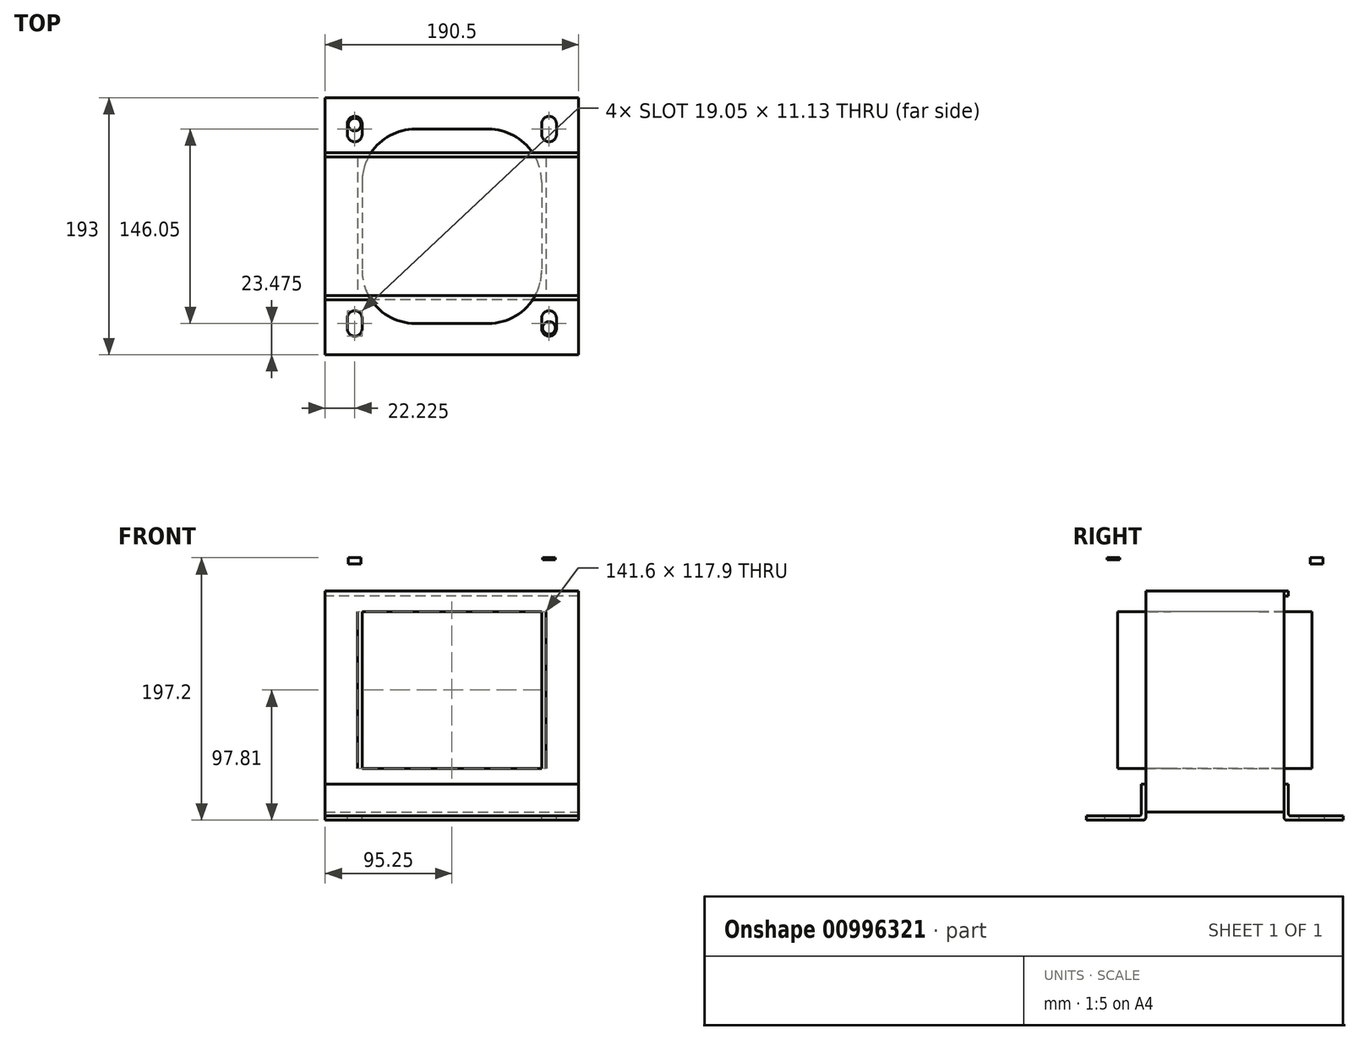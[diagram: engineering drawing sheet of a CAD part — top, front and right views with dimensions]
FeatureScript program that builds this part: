
annotation { "Feature Type Name" : "Feature", "Feature Type Description" : "" }
export const myFeature = defineFeature(function(context is Context, id is Id, definition is map)
    precondition{}
    {
        {
            var Q0;
            Q0=qCreatedBy(makeId("Front.planeOp"),FACE);
            var sketch = newSketch(context, id + "F0", { "sketchPlane" : qUnion([Q0])});
            skLineSegment(sketch, "E0.bottom", {"start": v(-95.25, -91.61) * mm, "end": v(95.25, -91.61) * mm});
            skLineSegment(sketch, "E0.top", {"start": v(-95.25, 91.61) * mm, "end": v(95.25, 91.61) * mm});
            skLineSegment(sketch, "E0.left", {"start": v(-95.25, -91.61) * mm, "end": v(-95.25, 91.61) * mm});
            skLineSegment(sketch, "E0.right", {"start": v(95.25, -91.61) * mm, "end": v(95.25, 91.61) * mm});
            skPoint(sketch, "E0.middle", {"position": v(0, 0) * mm});
            skSolve(sketch);
        }
        {
            var Q0;
            Q0=makeQuery(id+"F0.imprint","IMPRINT",FACE,{"disambiguationData":[TD([[makeQuery(id+"F0.imprint","IMPRINT",EDGE,{"derivedFrom":sQuery(id+"F0.wireOp",EDGE,"E0.bottom")}),1.0]])]});
            extrude(context, id + "F1", {"entities" : qUnion([Q0]), "depth" : 104 * mm, "offsetDistance" : 25 * mm});
        }
        {
            var Q0;
            Q0=makeQuery(id+"F1.opExtrude","SWEPT_FACE",FACE,{"disambiguationData":[OSD([sQuery(id+"F0.wireOp",EDGE,"E0.left")])]});
            var sketch = newSketch(context, id + "F2", { "sketchPlane" : qUnion([Q0])});
            skLineSegment(sketch, "E1.bottom", {"start": v(104, -70.61) * mm, "end": v(107.2, -70.61) * mm});
            skLineSegment(sketch, "E1.left", {"start": v(104, -70.61) * mm, "end": v(104, -94.61) * mm});
            skLineSegment(sketch, "E1.right", {"start": v(107.2, -70.61) * mm, "end": v(107.2, -92.61) * mm});
            skLineSegment(sketch, "E2.bottom", {"start": v(109.2, -94.61) * mm, "end": v(148.5, -94.61) * mm});
            skLineSegment(sketch, "E2.top", {"start": v(106, -97.81) * mm, "end": v(148.5, -97.81) * mm});
            skLineSegment(sketch, "E2.left", {"start": v(104, -94.61) * mm, "end": v(104, -95.81) * mm});
            skLineSegment(sketch, "E2.right", {"start": v(148.5, -94.61) * mm, "end": v(148.5, -97.81) * mm});
            skPoint(sketch, "E3.visualSharp", {"position": v(104, -97.81) * mm});
            skArc(sketch, "E3.filletArc", {"start": v(104, -95.81) * mm, "mid": v(104.59, -97.23) * mm, "end": v(106, -97.82) * mm});
            skPoint(sketch, "E4.visualSharp", {"position": v(107.2, -94.61) * mm});
            skArc(sketch, "E4.filletArc", {"start": v(107.2, -92.61) * mm, "mid": v(107.79, -94.03) * mm, "end": v(109.2, -94.62) * mm});
            skArc(sketch, "E5.MirrorCS", {"start": v(107.2, 92.62) * mm, "mid": v(107.79, 94.03) * mm, "end": v(109.2, 94.62) * mm});
            skArc(sketch, "E6.MirrorCS", {"start": v(104, 95.82) * mm, "mid": v(104.59, 97.23) * mm, "end": v(106, 97.82) * mm});
            skLineSegment(sketch, "E7.MirrorCS", {"start": v(104, 94.62) * mm, "end": v(104, 95.82) * mm});
            skLineSegment(sketch, "E8.MirrorCS", {"start": v(104, 70.62) * mm, "end": v(107.2, 70.62) * mm});
            skLineSegment(sketch, "E9.MirrorCS", {"start": v(148.5, 94.61) * mm, "end": v(148.5, 97.81) * mm});
            skPoint(sketch, "E10.MirrorP", {"position": v(107.2, 94.62) * mm});
            skLineSegment(sketch, "E11.MirrorCS", {"start": v(109.2, 94.62) * mm, "end": v(148.5, 94.61) * mm});
            skLineSegment(sketch, "E12.MirrorCS", {"start": v(104, 70.62) * mm, "end": v(104, 94.62) * mm});
            skLineSegment(sketch, "E13.MirrorCS", {"start": v(106, 97.82) * mm, "end": v(148.5, 97.81) * mm});
            skPoint(sketch, "E14.MirrorP", {"position": v(104, 97.82) * mm});
            skLineSegment(sketch, "E15.MirrorCS", {"start": v(107.2, 70.62) * mm, "end": v(107.2, 92.62) * mm});
            skLineSegment(sketch, "E16", {"start": v(52, 82.48) * mm, "end": v(52, 91.62) * mm, "construction": true});
            skLineSegment(sketch, "E17.MirrorCS", {"start": v(0, 94.62) * mm, "end": v(0, 95.82) * mm});
            skArc(sketch, "E18.MirrorCS", {"start": v(0, 95.82) * mm, "mid": v(-0.59, 97.23) * mm, "end": v(-2, 97.82) * mm});
            skArc(sketch, "E19.MirrorCS", {"start": v(-3.2, 92.62) * mm, "mid": v(-3.79, 94.03) * mm, "end": v(-5.2, 94.62) * mm});
            skLineSegment(sketch, "E20.MirrorCS", {"start": v(0, 70.62) * mm, "end": v(-3.2, 70.62) * mm});
            skLineSegment(sketch, "E21.MirrorCS", {"start": v(-44.5, 94.61) * mm, "end": v(-44.5, 97.81) * mm});
            skPoint(sketch, "E22.MirrorP", {"position": v(0, 97.82) * mm});
            skLineSegment(sketch, "E23.MirrorCS", {"start": v(-5.2, 94.62) * mm, "end": v(-44.5, 94.61) * mm});
            skLineSegment(sketch, "E24.MirrorCS", {"start": v(-3.2, 70.62) * mm, "end": v(-3.2, 92.62) * mm});
            skLineSegment(sketch, "E25.MirrorCS", {"start": v(-2, 97.82) * mm, "end": v(-44.5, 97.81) * mm});
            skLineSegment(sketch, "E26.MirrorCS", {"start": v(0, 70.62) * mm, "end": v(0, 94.62) * mm});
            skPoint(sketch, "E27.MirrorP", {"position": v(-3.2, 94.62) * mm});
            skLineSegment(sketch, "E28.bottom", {"start": v(-46.57, 99.39) * mm, "end": v(150.57, 99.39) * mm});
            skLineSegment(sketch, "E28.top", {"start": v(-46.57, 97.82) * mm, "end": v(150.57, 97.82) * mm});
            skLineSegment(sketch, "E28.left", {"start": v(-46.57, 99.39) * mm, "end": v(-46.57, 97.82) * mm});
            skLineSegment(sketch, "E28.right", {"start": v(150.57, 99.39) * mm, "end": v(150.57, 97.82) * mm});
            skSolve(sketch);
        }
        {
            var Q0;
            {var subQ2=sQuery(id+"F2.wireOp",EDGE,"E17.MirrorCS");Q0=makeQuery(id+"F2.imprint","IMPRINT",FACE,{"disambiguationData":[TD([[makeQuery(id+"F2.imprint","IMPRINT",EDGE,{"derivedFrom":subQ2}),1.0]])]});}
            var Q1;
            Q1=makeQuery(id+"F2.imprint","IMPRINT",FACE,{"disambiguationData":[TD([[makeQuery(id+"F2.imprint","IMPRINT",EDGE,{"derivedFrom":sQuery(id+"F2.wireOp",EDGE,"E5.MirrorCS")}),1.0]])]});
            var Q2;
            Q2=makeQuery(id+"F2.imprint","IMPRINT",FACE,{"disambiguationData":[TD([[makeQuery(id+"F2.imprint","IMPRINT",EDGE,{"derivedFrom":sQuery(id+"F2.wireOp",EDGE,"E28.bottom")}),-1.0]])]});
            var Q3;
            {var subQ4=sQuery(id+"F2.wireOp",EDGE,"E1.bottom");Q3=makeQuery(id+"F2.imprint","IMPRINT",FACE,{"disambiguationData":[TD([[makeQuery(id+"F2.imprint","IMPRINT",EDGE,{"derivedFrom":subQ4}),-1.0]])]});}
            var Q4;
            Q4=makeQuery(id+"F1.opExtrude","SWEPT_FACE",FACE,{"disambiguationData":[OSD([sQuery(id+"F0.wireOp",EDGE,"E0.right")])]});
            extrude(context, id + "F3", {"entities" : qUnion([Q0, Q1, Q2, Q3]), "endBound" : BoundingType.UP_TO_SURFACE, "oppositeDirection" : true, "depth" : 25 * mm, "endBoundEntityFace" : qUnion([Q4]), "offsetDistance" : 25 * mm});
        }
        {
            var Q0;
            Q0=makeQuery(id+"F1.opExtrude","CAP_EDGE",EDGE,{"disambiguationData":[OSD([sQuery(id+"F0.wireOp",EDGE,"E0.right")])],"isStart":false});
            cPoint(context, id + "F4", {"entities" : qUnion([Q0]), "parameter" : 0.5});
        }
        {
            var Q0;
            Q0=makeQuery(id+"F1.opExtrude","CAP_EDGE",EDGE,{"disambiguationData":[OSD([sQuery(id+"F0.wireOp",EDGE,"E0.right")])],"isStart":true});
            cPoint(context, id + "F5", {"entities" : qUnion([Q0]), "parameter" : 0.5});
        }
        {
            var Q0;
            Q0 = qCreatedBy(id + "F4" ,VERTEX);
            var Q1;
            Q1 = qCreatedBy(id + "F5" ,VERTEX);
            cPlane(context, id + "F6", {"entities" : qUnion([Q0, Q1]), "cplaneType" : CPlaneType.MID_PLANE, "offset" : 25 * mm, "width" : 150 * mm, "height" : 150 * mm});
        }
        {
            var Q0;
            Q0=makeQuery(id+"F3.opExtrude","SWEPT_BODY",BODY,{"disambiguationData":[OSD([sQuery(id+"F2.wireOp",EDGE,"E1.bottom"),sQuery(id+"F2.wireOp",EDGE,"E1.left"),sQuery(id+"F2.wireOp",EDGE,"E1.right"),sQuery(id+"F2.wireOp",EDGE,"E2.bottom"),sQuery(id+"F2.wireOp",EDGE,"E2.top"),sQuery(id+"F2.wireOp",EDGE,"E2.left"),sQuery(id+"F2.wireOp",EDGE,"E2.right")])]});
            var Q1;
            Q1=qCreatedBy(id+"F6.planeOp",FACE);
            mirror(context, id + "F7", {"entities" : qUnion([Q0]), "mirrorPlane" : qUnion([Q1])});
        }
        {
            var Q0;
            Q0=makeQuery(id+"F3.opExtrude","SWEPT_FACE",FACE,{"disambiguationData":[OSD([sQuery(id+"F2.wireOp",EDGE,"E2.bottom")])]});
            var sketch = newSketch(context, id + "F8", { "sketchPlane" : qUnion([Q0])});
            skLineSegment(sketch, "E29", {"start": v(-73.02, 44.5) * mm, "end": v(-73.03, -148.5) * mm, "construction": true});
            skArc(sketch, "E30", {"start": v(-67.46, -121.06) * mm, "mid": v(-73.03, -115.5) * mm, "end": v(-78.59, -121.06) * mm});
            skLineSegment(sketch, "E31", {"start": v(-73.03, -115.5) * mm, "end": v(-73.03, -134.55) * mm, "construction": true});
            skArc(sketch, "E32", {"start": v(-78.59, -128.99) * mm, "mid": v(-73.03, -134.55) * mm, "end": v(-67.46, -128.99) * mm});
            skLineSegment(sketch, "E33", {"start": v(-67.46, -121.06) * mm, "end": v(-67.46, -128.99) * mm});
            skLineSegment(sketch, "E34", {"start": v(-78.59, -121.06) * mm, "end": v(-67.46, -121.06) * mm, "construction": true});
            skLineSegment(sketch, "E35", {"start": v(-78.59, -128.99) * mm, "end": v(-67.46, -128.99) * mm, "construction": true});
            skLineSegment(sketch, "E36", {"start": v(-78.59, -121.06) * mm, "end": v(-78.59, -128.99) * mm});
            skPoint(sketch, "E37", {"position": v(-73.03, -125.03) * mm});
            skPoint(sketch, "E38", {"position": v(-73.02, -52) * mm});
            skLineSegment(sketch, "E39", {"start": v(-73.02, -52) * mm, "end": v(-45.17, -52) * mm, "construction": true});
            skArc(sketch, "E40.MirrorCS", {"start": v(-78.59, 24.99) * mm, "mid": v(-73.03, 30.55) * mm, "end": v(-67.46, 24.99) * mm});
            skLineSegment(sketch, "E41.MirrorCS", {"start": v(-78.59, 17.06) * mm, "end": v(-78.59, 24.99) * mm});
            skLineSegment(sketch, "E42.MirrorCS", {"start": v(-67.46, 17.06) * mm, "end": v(-67.46, 24.99) * mm});
            skArc(sketch, "E43.MirrorCS", {"start": v(-67.46, 17.06) * mm, "mid": v(-73.03, 11.5) * mm, "end": v(-78.59, 17.06) * mm});
            skLineSegment(sketch, "E44", {"start": v(0, 0) * mm, "end": v(0, -57.64) * mm, "construction": true});
            skLineSegment(sketch, "E45.MirrorCS", {"start": v(73.03, -115.5) * mm, "end": v(73.03, -134.55) * mm, "construction": true});
            skLineSegment(sketch, "E46.MirrorCS", {"start": v(78.59, -121.06) * mm, "end": v(67.46, -121.06) * mm, "construction": true});
            skLineSegment(sketch, "E47.MirrorCS", {"start": v(78.59, -128.99) * mm, "end": v(67.46, -128.99) * mm, "construction": true});
            skLineSegment(sketch, "E48.MirrorCS", {"start": v(67.46, -121.06) * mm, "end": v(67.46, -128.99) * mm});
            skPoint(sketch, "E49.MirrorP", {"position": v(73.03, -125.03) * mm});
            skArc(sketch, "E50.MirrorCS", {"start": v(67.46, -121.06) * mm, "mid": v(73.03, -115.5) * mm, "end": v(78.59, -121.06) * mm});
            skArc(sketch, "E51.MirrorCS", {"start": v(78.59, -128.99) * mm, "mid": v(73.03, -134.55) * mm, "end": v(67.46, -128.99) * mm});
            skLineSegment(sketch, "E52.MirrorCS", {"start": v(78.59, -121.06) * mm, "end": v(78.59, -128.99) * mm});
            skLineSegment(sketch, "E53.MirrorCS", {"start": v(67.46, 17.06) * mm, "end": v(67.46, 24.99) * mm});
            skLineSegment(sketch, "E54.MirrorCS", {"start": v(78.59, 17.06) * mm, "end": v(78.59, 24.99) * mm});
            skArc(sketch, "E55.MirrorCS", {"start": v(78.59, 24.99) * mm, "mid": v(73.03, 30.55) * mm, "end": v(67.46, 24.99) * mm});
            skArc(sketch, "E56.MirrorCS", {"start": v(67.46, 17.06) * mm, "mid": v(73.03, 11.5) * mm, "end": v(78.59, 17.06) * mm});
            skLineSegment(sketch, "E57", {"start": v(73.03, 24.99) * mm, "end": v(73.03, -128.99) * mm, "construction": true});
            skSolve(sketch);
        }
        {
            var Q0;
            Q0 = qSketchRegion(id + "F8", true);
            extrude(context, id + "F9", {"entities" : qUnion([Q0]), "operationType" : NewBodyOperationType.REMOVE, "endBound" : BoundingType.THROUGH_ALL, "oppositeDirection" : true, "depth" : 25 * mm, "offsetDistance" : 25 * mm});
        }
        {
            var Q0;
            Q0=makeQuery(id+"F1.opExtrude","CAP_FACE",FACE,{"disambiguationData":[OSD([sQuery(id+"F0.wireOp",EDGE,"E0.bottom"),sQuery(id+"F0.wireOp",EDGE,"E0.top"),sQuery(id+"F0.wireOp",EDGE,"E0.left"),sQuery(id+"F0.wireOp",EDGE,"E0.right")])],"isStart":false});
            var sketch = newSketch(context, id + "F10", { "sketchPlane" : qUnion([Q0])});
            skLineSegment(sketch, "E58.bottom", {"start": v(-70.8, 58.95) * mm, "end": v(70.8, 58.95) * mm});
            skLineSegment(sketch, "E58.top", {"start": v(-70.8, -58.95) * mm, "end": v(70.8, -58.95) * mm});
            skLineSegment(sketch, "E58.left", {"start": v(-70.8, 58.95) * mm, "end": v(-70.8, -58.95) * mm});
            skLineSegment(sketch, "E58.right", {"start": v(70.8, 58.95) * mm, "end": v(70.8, -58.95) * mm});
            skPoint(sketch, "E58.middle", {"position": v(0, 0) * mm});
            skSolve(sketch);
        }
        {
            var Q0;
            Q0=makeQuery(id+"F10.imprint","IMPRINT",FACE,{"disambiguationData":[TD([[makeQuery(id+"F10.imprint","IMPRINT",EDGE,{"derivedFrom":sQuery(id+"F10.wireOp",EDGE,"E58.bottom")}),-1.0]])]});
            extrude(context, id + "F11", {"entities" : qUnion([Q0]), "operationType" : NewBodyOperationType.REMOVE, "endBound" : BoundingType.THROUGH_ALL, "oppositeDirection" : true, "depth" : 25 * mm, "offsetDistance" : 25 * mm});
        }
        {
            var Q0;
            Q0=makeQuery(id+"F11.boolean.opBoolean","COPY",FACE,{"derivedFrom":makeQuery(id+"F11.opExtrude","SWEPT_FACE",FACE,{"disambiguationData":[OSD([sQuery(id+"F10.wireOp",EDGE,"E58.top")])]})});
            var sketch = newSketch(context, id + "F12", { "sketchPlane" : qUnion([Q0])});
            skPoint(sketch, "E59", {"position": v(-70.8, -104) * mm});
            skPoint(sketch, "E60", {"position": v(70.8, 0) * mm});
            skPoint(sketch, "E61", {"position": v(-70.8, 0) * mm});
            skPoint(sketch, "E62", {"position": v(70.8, -104) * mm});
            skLineSegment(sketch, "E63", {"start": v(-70.8, -104) * mm, "end": v(70.8, 0) * mm, "construction": true});
            skLineSegment(sketch, "E64", {"start": v(-70.8, 0) * mm, "end": v(70.8, -104) * mm, "construction": true});
            skLineSegment(sketch, "E65.bottom", {"start": v(-27.5, -125.02) * mm, "end": v(27.5, -125.02) * mm});
            skLineSegment(sketch, "E65.top", {"start": v(-27.5, 21.03) * mm, "end": v(27.5, 21.03) * mm});
            skLineSegment(sketch, "E65.left", {"start": v(-67.5, -85.02) * mm, "end": v(-67.5, -18.97) * mm});
            skLineSegment(sketch, "E65.right", {"start": v(67.5, -85.02) * mm, "end": v(67.5, -18.97) * mm});
            skPoint(sketch, "E65.middle", {"position": v(0, -52) * mm});
            skPoint(sketch, "E66", {"position": v(-67.5, -104) * mm});
            skPoint(sketch, "E67", {"position": v(67.5, -104) * mm});
            skPoint(sketch, "E68.visualSharp", {"position": v(-67.5, -125.02) * mm});
            skArc(sketch, "E68.filletArc", {"start": v(-67.5, -85.02) * mm, "mid": v(-55.78, -113.3) * mm, "end": v(-27.5, -125.02) * mm});
            skPoint(sketch, "E69.visualSharp", {"position": v(67.5, -125.02) * mm});
            skArc(sketch, "E69.filletArc", {"start": v(27.5, -125.02) * mm, "mid": v(55.78, -113.3) * mm, "end": v(67.5, -85.02) * mm});
            skPoint(sketch, "E70", {"position": v(-67.5, 0) * mm});
            skPoint(sketch, "E71", {"position": v(67.5, 0) * mm});
            skPoint(sketch, "E72.visualSharp", {"position": v(67.5, 21.03) * mm});
            skArc(sketch, "E72.filletArc", {"start": v(67.5, -18.97) * mm, "mid": v(55.78, 9.3) * mm, "end": v(27.5, 21.03) * mm});
            skPoint(sketch, "E73.visualSharp", {"position": v(-67.5, 21.03) * mm});
            skArc(sketch, "E73.filletArc", {"start": v(-27.5, 21.03) * mm, "mid": v(-55.78, 9.3) * mm, "end": v(-67.5, -18.97) * mm});
            skSolve(sketch);
        }
        {
            var Q0;
            {var subQ1=sQuery(id+"F12.wireOp",EDGE,"E65.left");Q0=makeQuery(id+"F12.imprint","IMPRINT",FACE,{"disambiguationData":[TD([[makeQuery(id+"F12.imprint","IMPRINT",EDGE,{"derivedFrom":subQ1}),-1.0]])]});}
            var Q1;
            {var subQ0=sQuery(id+"F12.wireOp",EDGE,"E65.top");Q1=makeQuery(id+"F12.imprint","IMPRINT",FACE,{"disambiguationData":[TD([[makeQuery(id+"F12.imprint","IMPRINT",EDGE,{"derivedFrom":subQ0}),-1.0]])]});}
            var Q2;
            {var subQ0=sQuery(id+"F12.wireOp",EDGE,"E65.bottom");Q2=makeQuery(id+"F12.imprint","IMPRINT",FACE,{"disambiguationData":[TD([[makeQuery(id+"F12.imprint","IMPRINT",EDGE,{"derivedFrom":subQ0}),1.0]])]});}
            var Q3;
            Q3=makeQuery(id+"F11.boolean.opBoolean","COPY",FACE,{"derivedFrom":makeQuery(id+"F11.opExtrude","SWEPT_FACE",FACE,{"disambiguationData":[OSD([sQuery(id+"F10.wireOp",EDGE,"E58.bottom")])]})});
            extrude(context, id + "F13", {"entities" : qUnion([Q0, Q1, Q2]), "endBound" : BoundingType.UP_TO_SURFACE, "depth" : 25 * mm, "endBoundEntityFace" : qUnion([Q3]), "offsetDistance" : 25 * mm});
        }
        {
            var Q0;
            Q0=makeQuery(id+"F3.opExtrude","SWEPT_FACE",FACE,{"disambiguationData":[OSD([sQuery(id+"F2.wireOp",EDGE,"E28.bottom")])]});
            var sketch = newSketch(context, id + "F14", { "sketchPlane" : qUnion([Q0])});
            skCircle(sketch, "E74", {"center": v(-73.03, -128.35) * mm, "radius": 4.76 * mm});
            skPoint(sketch, "E75.0", {"position": v(0, -150.57) * mm});
            skPoint(sketch, "E76.0", {"position": v(-95.25, -52) * mm});
            skLineSegment(sketch, "E77", {"start": v(0, -150.57) * mm, "end": v(0, -164.73) * mm, "construction": true});
            skLineSegment(sketch, "E78", {"start": v(-95.25, -52) * mm, "end": v(-111.7, -52) * mm, "construction": true});
            skCircle(sketch, "E79.MirrorC", {"center": v(73.03, -128.35) * mm, "radius": 4.76 * mm});
            skCircle(sketch, "E80.MirrorC", {"center": v(-73.03, 24.35) * mm, "radius": 4.76 * mm});
            skCircle(sketch, "E81.MirrorC", {"center": v(73.03, 24.35) * mm, "radius": 4.76 * mm});
            skSolve(sketch);
        }
        {
            var Q0;
            Q0=makeQuery(id+"F14.imprint","IMPRINT",FACE,{"disambiguationData":[TD([[makeQuery(id+"F14.imprint","IMPRINT",EDGE,{"derivedFrom":sQuery(id+"F14.wireOp",EDGE,"E80.MirrorC")}),-1.0]])]});
            var Q1;
            Q1=makeQuery(id+"F14.imprint","IMPRINT",FACE,{"disambiguationData":[TD([[makeQuery(id+"F14.imprint","IMPRINT",EDGE,{"derivedFrom":sQuery(id+"F14.wireOp",EDGE,"E81.MirrorC")}),1.0]])]});
            var Q2;
            Q2=makeQuery(id+"F14.imprint","IMPRINT",FACE,{"disambiguationData":[TD([[makeQuery(id+"F14.imprint","IMPRINT",EDGE,{"derivedFrom":sQuery(id+"F14.wireOp",EDGE,"E74")}),1.0]])]});
            var Q3;
            Q3=makeQuery(id+"F14.imprint","IMPRINT",FACE,{"disambiguationData":[TD([[makeQuery(id+"F14.imprint","IMPRINT",EDGE,{"derivedFrom":sQuery(id+"F14.wireOp",EDGE,"E79.MirrorC")}),-1.0]])]});
            extrude(context, id + "F15", {"entities" : qUnion([Q0, Q1, Q2, Q3]), "operationType" : NewBodyOperationType.REMOVE, "oppositeDirection" : true, "depth" : 25 * mm, "offsetDistance" : 25 * mm});
        }
    });
